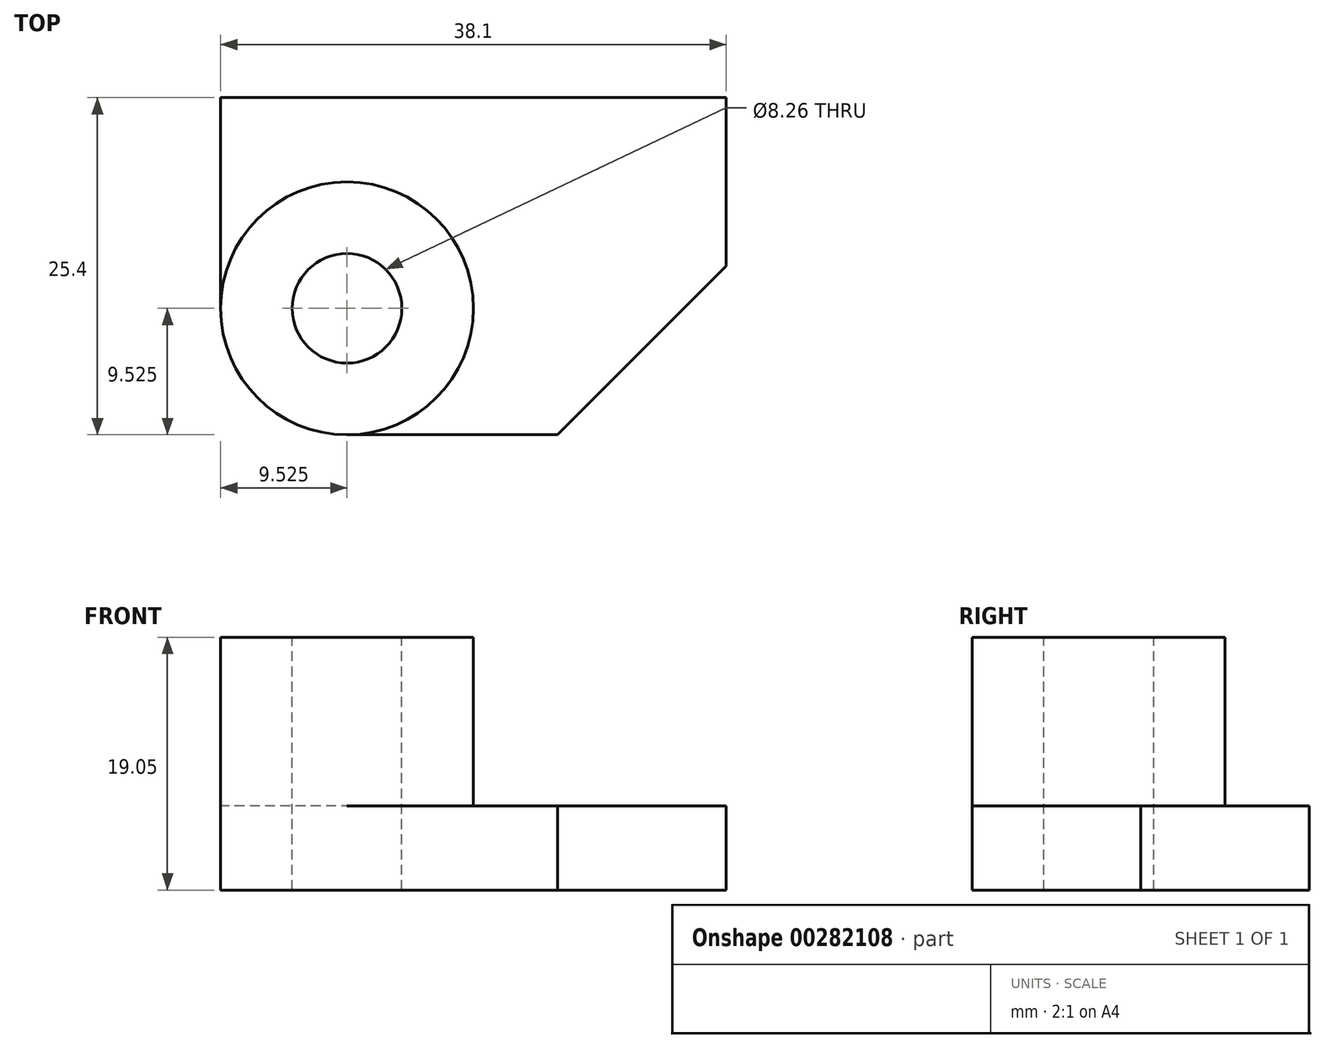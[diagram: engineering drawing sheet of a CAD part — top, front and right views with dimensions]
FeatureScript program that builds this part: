
annotation { "Feature Type Name" : "Feature", "Feature Type Description" : "" }
export const myFeature = defineFeature(function(context is Context, id is Id, definition is map)
    precondition{}
    {
        {
            var Q0;
            Q0=qCreatedBy(makeId("Top.planeOp"),FACE);
            var sketch = newSketch(context, id + "F0", { "sketchPlane" : qUnion([Q0])});
            skLineSegment(sketch, "E0", {"start": v(0, 0) * mm, "end": v(0, 25.4) * mm});
            skLineSegment(sketch, "E1", {"start": v(0, 25.4) * mm, "end": v(38.1, 25.4) * mm});
            skLineSegment(sketch, "E2", {"start": v(38.1, 25.4) * mm, "end": v(38.1, 12.7) * mm});
            skLineSegment(sketch, "E3", {"start": v(38.1, 12.7) * mm, "end": v(25.4, 0) * mm});
            skLineSegment(sketch, "E4", {"start": v(25.4, 0) * mm, "end": v(0, 0) * mm});
            skSolve(sketch);
        }
        {
            var Q0;
            Q0 = qSketchRegion(id + "F0", true);
            extrude(context, id + "F1", {"entities" : qUnion([Q0]), "depth" : 6.35 * mm});
        }
        {
            var Q0;
            Q0=makeQuery(id+"F1.opExtrude","CAP_FACE",FACE,{"disambiguationData":[OSD([sQuery(id+"F0.wireOp",EDGE,"E0"),sQuery(id+"F0.wireOp",EDGE,"E1"),sQuery(id+"F0.wireOp",EDGE,"E2"),sQuery(id+"F0.wireOp",EDGE,"E3"),sQuery(id+"F0.wireOp",EDGE,"E4")])],"isStart":false});
            var sketch = newSketch(context, id + "F2", { "sketchPlane" : qUnion([Q0])});
            skPoint(sketch, "E5.startSnap0", {"position": v(0, 12.7) * mm});
            skLineSegment(sketch, "E6", {"start": v(12.7, 33.45) * mm, "end": v(12.7, -17.35) * mm, "construction": true});
            skPoint(sketch, "E6.startSnap0", {"position": v(12.7, 0) * mm});
            skCircle(sketch, "E7", {"center": v(9.53, 9.53) * mm, "radius": 4.13 * mm});
            skCircle(sketch, "E8", {"center": v(9.53, 9.53) * mm, "radius": 9.53 * mm});
            skSolve(sketch);
        }
        {
            var Q0;
            Q0=makeQuery(id+"F2.imprint","IMPRINT",FACE,{"disambiguationData":[TD([[makeQuery(id+"F2.imprint","IMPRINT",EDGE,{"derivedFrom":sQuery(id+"F2.wireOp",EDGE,"E7")}),1.0]])]});
            extrude(context, id + "F3", {"entities" : qUnion([Q0]), "operationType" : NewBodyOperationType.REMOVE, "endBound" : BoundingType.THROUGH_ALL, "oppositeDirection" : true, "depth" : 12.7 * mm});
        }
        {
            var Q0;
            Q0 = qSketchRegion(id + "F2", true);
            extrude(context, id + "F4", {"entities" : qUnion([Q0]), "operationType" : NewBodyOperationType.ADD, "depth" : 12.7 * mm});
        }
        {
            var Q0;
            {var subQ0=sQuery(id+"F0.wireOp",EDGE,"E0");var subQ1=sQuery(id+"F0.wireOp",EDGE,"E4");var subQ2=makeQuery(id+"F1.opExtrude","CAP_FACE",FACE,{"disambiguationData":[OSD([subQ0,sQuery(id+"F0.wireOp",EDGE,"E1"),sQuery(id+"F0.wireOp",EDGE,"E2"),sQuery(id+"F0.wireOp",EDGE,"E3"),subQ1])],"isStart":false});Q0=makeQuery(id+"F4.boolean.opBoolean","SPLIT",FACE,{"disambiguationData":[TD([makeQuery(id+"F1.opExtrude","SWEPT_FACE",FACE,{"disambiguationData":[OSD([subQ0])]}),subQ2,makeQuery(id+"F1.opExtrude","SWEPT_FACE",FACE,{"disambiguationData":[OSD([subQ1])]}),makeQuery(id+"F4.opExtrude","SWEPT_FACE",FACE,{"disambiguationData":[OSD([sQuery(id+"F2.wireOp",EDGE,"E8")])]})])],"derivedFrom":subQ2});}
            extrude(context, id + "F5", {"entities" : qUnion([Q0]), "operationType" : NewBodyOperationType.REMOVE, "oppositeDirection" : true, "depth" : 25.4 * mm});
        }
    });
